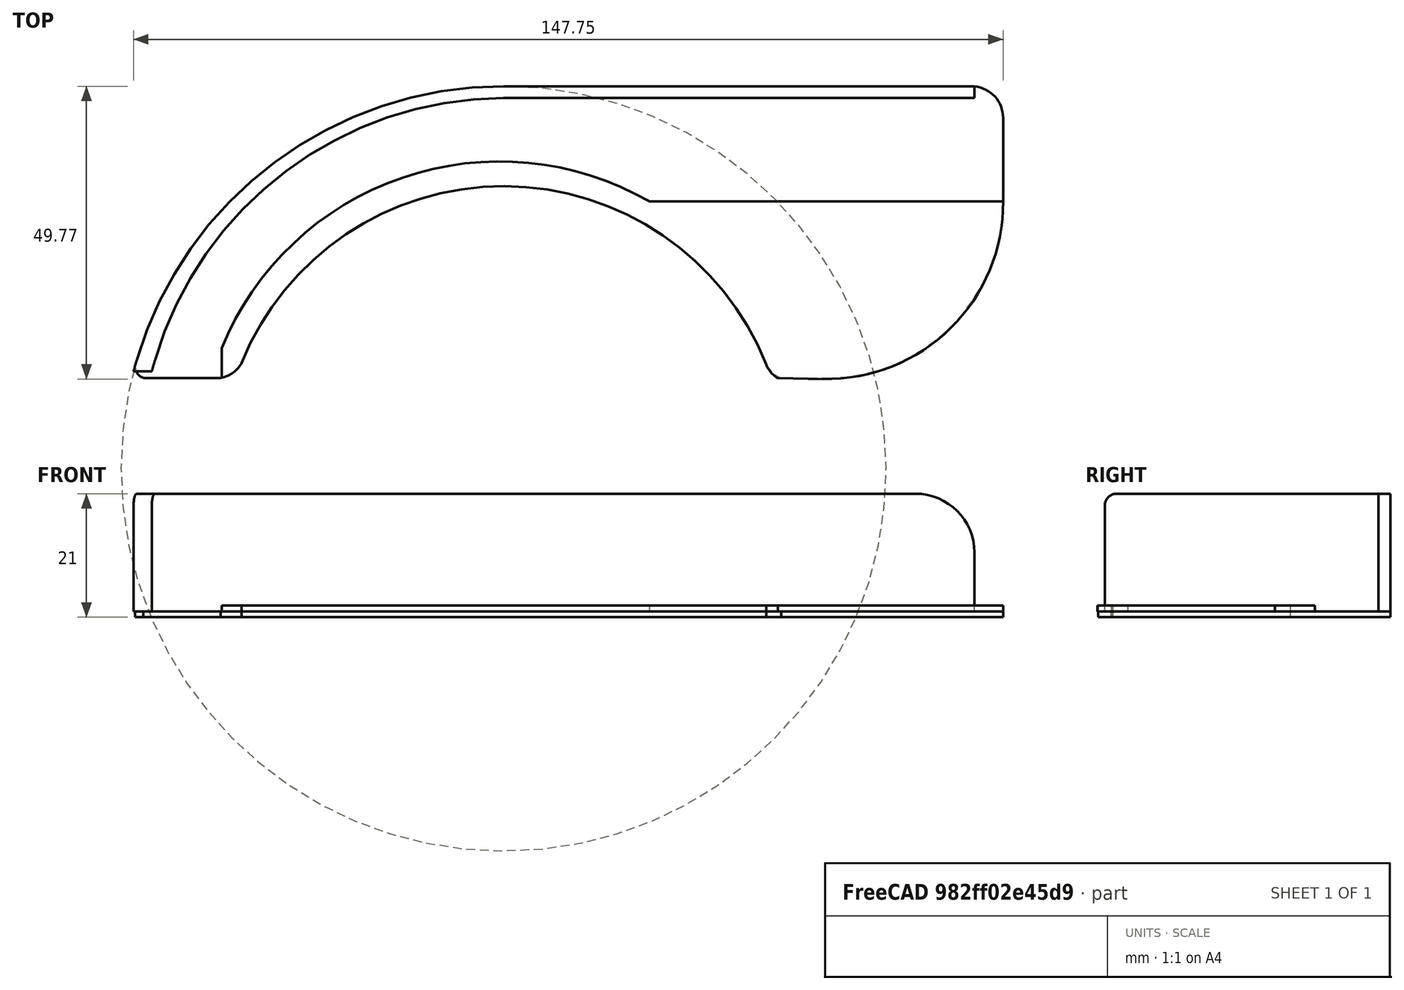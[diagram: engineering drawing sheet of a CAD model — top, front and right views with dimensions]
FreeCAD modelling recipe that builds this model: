
FCSTD DOCUMENT  (FreeCAD 0.16R)
Label: V1
License: All rights reserved
LicenseURL: http://en.wikipedia.org/wiki/All_rights_reserved
objects: Sketcher::SketchObject×3, PartDesign::Pad×3, Mesh::Feature×3, PartDesign::Fillet×2
note: 11 computed .brp shape members not serialized (recipe doc carries the construction recipe); baked Part::Feature solids carry a one-line shape summary decoded from their .brp

FEATURE [Sketcher::SketchObject] Sketch
  sketch-geometry (11):
    g0: ArcOfCircle CenterX=0 CenterY=0 CenterZ=0 NormalX=0 NormalY=0 NormalZ=1 Radius=65 StartAngle=1.5708 EndAngle=2.86744
    g1: ArcOfCircle CenterX=0 CenterY=0 CenterZ=0 NormalX=0 NormalY=0 NormalZ=1 Radius=48 StartAngle=0.377003 EndAngle=2.75854
    g2: LineSegment StartX=2.40667e-07 StartY=65 StartZ=0 EndX=79.4942 EndY=65 EndZ=0
    g3: LineSegment StartX=47.168 StartY=15.3736 StartZ=0 EndX=54.9232 EndY=15.3842 EndZ=0
    g4: LineSegment StartX=84.8824 StartY=59.6118 StartZ=0 EndX=84.8824 EndY=45.3841 EndZ=0
    g5: ArcOfCircle CenterX=54.8824 CenterY=45.3841 CenterZ=0 NormalX=0 NormalY=0 NormalZ=1 Radius=30 StartAngle=4.71375 EndAngle=6.28319
    g6: ArcOfCircle CenterX=79.4942 CenterY=59.6118 CenterZ=0 NormalX=0 NormalY=0 NormalZ=1 Radius=5.38817 StartAngle=0 EndAngle=1.5708
    g7: ArcOfCircle CenterX=49.0502 CenterY=20.0058 CenterZ=0 NormalX=0 NormalY=0 NormalZ=1 Radius=5 StartAngle=3.62755 EndAngle=4.32643
    g8: ArcOfCircle CenterX=-60.5912 CenterY=17.3257 CenterZ=0 NormalX=0 NormalY=0 NormalZ=1 Radius=2 StartAngle=3.00536 EndAngle=4.40537
    g9: ArcOfCircle CenterX=-48.9002 CenterY=20.3538 CenterZ=0 NormalX=0 NormalY=0 NormalZ=1 Radius=5 StartAngle=4.8743 EndAngle=5.77943
    g10: LineSegment StartX=-61.1956 StartY=15.4192 StartZ=0 EndX=-48.0942 EndY=15.4192 EndZ=0
  constraints (35):
    c: Radius(g0) = 65
    c: Coincident(g-1,g0)
    c: PointOnObject(g1,g-2)
    c: Coincident(g1,g-1)
    c: Radius(g1) = 48
    c: Horizontal(g2)
    c: Coincident(g0,g2)
    c: Vertical(g4)
    c: Tangent(g4,g5) = 1.5708
    c: Tangent(g3,g5) = -1.5708
    c: Tangent(g4,g6) = 1.5708
    c: Tangent(g2,g6) = 1.5708
    c: Radius(g7) = 5
    c: Radius(g9) = 5
    c: Radius(g8) = 2
    c: Coincident(g3,g7)
    c: Coincident(g1,g7)
    c: Coincident(g10,g9)
    c: Coincident(g1,g9)
    c: Coincident(g10,g8)
    c: Coincident(g0,g8)
    c: Distance(g10) = 13.1014
    c: Distance(g2) = 79.4942
    c: Distance(g3) = 7.75526
    c: Distance(g4) = 14.2277
    c: Radius(g5) = 30
    c: Radius(g6) = 5.38817
    c: DistanceY(g-1,g2) = 65
    c: DistanceY(g3) = 15.3736
    c: DistanceY(g9) = 15.4192
    c: DistanceY(g0) = 17.5973
    c: DistanceY(g1) = 17.9402
    c: DistanceY(g8) = 15.4192
    c: DistanceY(g1) = 17.6705
    c: DistanceX(g8) = -61.1956
FEATURE [Sketcher::SketchObject] Sketch002
  Placement = pos=(0,0,1) rot=(0,0,1;0rad)
  sketch-geometry (8):
    g0: ArcOfCircle CenterX=0 CenterY=0 CenterZ=0 NormalX=0 NormalY=0 NormalZ=1 Radius=48 StartAngle=0.377003 EndAngle=2.75854
    g1: LineSegment StartX=46.5747 StartY=15.3736 StartZ=0 EndX=54.3287 EndY=15.2303 EndZ=0
    g2: ArcOfCircle CenterX=54.883 CenterY=45.2252 CenterZ=0 NormalX=0 NormalY=0 NormalZ=1 Radius=30 StartAngle=4.69391 EndAngle=6.28891
    g3: ArcOfCircle CenterX=49.2401 CenterY=19.6039 CenterZ=0 NormalX=0 NormalY=0 NormalZ=1 Radius=5 StartAngle=3.53863 EndAngle=4.15015
    g4: ArcOfCircle CenterX=-48.9021 CenterY=20.3504 CenterZ=0 NormalX=0 NormalY=0 NormalZ=1 Radius=5 StartAngle=4.91142 EndAngle=5.7802
    g5: ArcOfCircle CenterX=-0.679134 CenterY=1.21593 CenterZ=0 NormalX=0 NormalY=0 NormalZ=1 Radius=51 StartAngle=1.04774 EndAngle=2.75491
    g6: LineSegment StartX=84.8825 StartY=45.397 StartZ=0 EndX=24.797 EndY=45.397 EndZ=0
    g7: LineSegment StartX=-47.9135 StartY=20.4491 StartZ=0 EndX=-47.9135 EndY=15.4491 EndZ=0
  constraints (29):
    c: PointOnObject(g0,g-2)
    c: Coincident(g0,g-1)
    c: Radius(g0) = 48
    c: Tangent(g1,g2) = -1.5708
    c: Radius(g3) = 5
    c: Radius(g4) = 5
    c: Coincident(g1,g3)
    c: Coincident(g0,g3)
    c: Coincident(g0,g4)
    c: Distance(g1) = 7.75526
    c: Radius(g2) = 30
    c: DistanceY(g1) = 15.3736
    c: DistanceY(g0) = 17.9402
    c: DistanceY(g0) = 17.6705
    c: DistanceX(g4,g5) = 0
    c: DistanceX(g5) = -47.9135
    c: DistanceY(g4) = 15.4491
    c: DistanceY(g4,g5) = 5
    c: Radius(g5) = 51
    c: Coincident(g6,g2)
    c: Horizontal(g6)
    c: Coincident(g5,g6)
    c: Vertical(g7)
    c: Coincident(g7,g5)
    c: Coincident(g7,g4)
    c: DistanceX(g5) = 24.797
    c: DistanceY(g5) = 45.397
    c: DistanceX(g2) = 84.8825
    c: DistanceY(g1) = 15.2303
FEATURE [PartDesign::Pad] Pad002  label="Stiffener"
  Length = 1
  Length2 = 100
  Placement = pos=(0,0,1) rot=(0,0,1;0rad)
  Sketch = -> Sketch002
  Type = 0
FEATURE [PartDesign::Pad] Pad  label="Faceplate"
  Length = 1
  Length2 = 100
  Sketch = -> Sketch
  Type = 0
FEATURE [Sketcher::SketchObject] Sketch001
  Placement = pos=(0,0,1) rot=(0,0,1;0rad)
  Support = -> Pad [Face13]
  sketch-geometry (6):
    g0: ArcOfCircle CenterX=0 CenterY=0 CenterZ=0 NormalX=0 NormalY=0 NormalZ=1 Radius=65 StartAngle=1.5708 EndAngle=2.88461
    g1: LineSegment StartX=6.04881e-05 StartY=65 StartZ=0 EndX=80.0001 EndY=65 EndZ=0
    g2: LineSegment StartX=80.0001 StartY=63 StartZ=0 EndX=6.04881e-05 EndY=63 EndZ=0
    g3: LineSegment StartX=80.0001 StartY=65 StartZ=0 EndX=80.0001 EndY=63 EndZ=0
    g4: ArcOfCircle CenterX=0.26057 CenterY=1.00055 CenterZ=0 NormalX=0 NormalY=0 NormalZ=1 Radius=62 StartAngle=1.575 EndAngle=2.88858
    g5: LineSegment StartX=-62.8655 StartY=16.5204 StartZ=0 EndX=-59.7655 EndY=16.5204 EndZ=0
  constraints (19):
    c: Radius(g0) = 65
    c: Coincident(g-1,g0)
    c: Horizontal(g1)
    c: Coincident(g0,g1)
    c: DistanceY(g-1,g1) = 65
    c: Horizontal(g2)
    c: Equal(g2,g1)
    c: DistanceX(g0,g2) = 0
    c: Coincident(g3,g2)
    c: Coincident(g3,g1)
    c: DistanceY(g2,g1) = 2
    c: Radius(g4) = 62
    c: Coincident(g4,g2)
    c: DistanceX(g0,g4) = 3.1
    c: DistanceY(g4,g0) = 0
    c: DistanceY(g-1,g0) = 16.5204
    c: Coincident(g4,g5)
    c: Coincident(g5,g0)
    c: Distance(g1) = 80
FEATURE [PartDesign::Pad] Pad004  label="Connector"
  Length = 20
  Length2 = 100
  Sketch = -> Sketch001
  Type = 0
FEATURE [PartDesign::Fillet] Fillet
  Base = -> Pad004 [Edge52]
  Radius = 10
FEATURE [PartDesign::Fillet] Fillet001
  Base = -> Fillet [Edge25]
  Radius = 2
FEATURE [Mesh::Feature] Mesh  label="Stiffener (Meshed)"
FEATURE [Mesh::Feature] Mesh001  label="Faceplate (Meshed)"
FEATURE [Mesh::Feature] Mesh002  label="Fillet001 (Meshed)"
